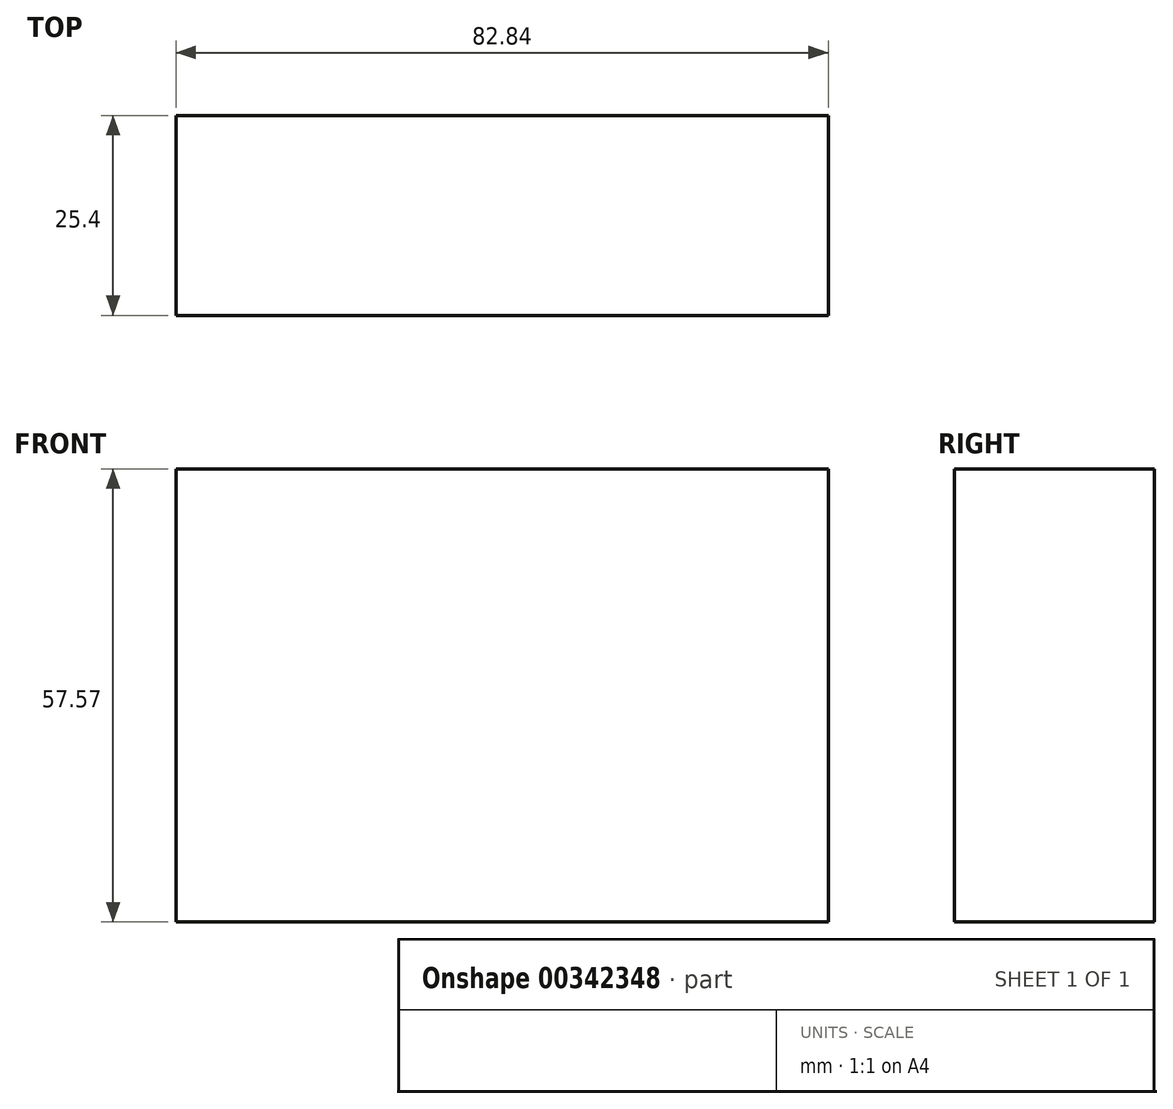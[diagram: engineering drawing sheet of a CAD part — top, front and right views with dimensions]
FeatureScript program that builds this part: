
annotation { "Feature Type Name" : "Feature", "Feature Type Description" : "" }
export const myFeature = defineFeature(function(context is Context, id is Id, definition is map)
    precondition{}
    {
        {
            var Q0;
            Q0=qCreatedBy(makeId("Front.planeOp"), FACE);
            var sketch = newSketch(context, id + "F0", { "sketchPlane" : qUnion([Q0])});
            skLineSegment(sketch, "E0.bottom", {"start": v(-56.2, 46.93) * mm, "end": v(26.65, 46.93) * mm});
            skLineSegment(sketch, "E0.top", {"start": v(-56.2, -10.64) * mm, "end": v(26.65, -10.64) * mm});
            skLineSegment(sketch, "E0.left", {"start": v(-56.2, 46.93) * mm, "end": v(-56.2, -10.64) * mm});
            skLineSegment(sketch, "E0.right", {"start": v(26.65, 46.93) * mm, "end": v(26.65, -10.64) * mm});
            skSolve(sketch);
        }
        {
            var Q0;
            Q0 = qSketchRegion(id + "F0", true);
            extrude(context, id + "F1", {"entities" : qUnion([Q0]), "depth" : 25.4 * mm, "offsetDistance" : 25.4 * mm});
        }
    });
